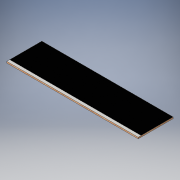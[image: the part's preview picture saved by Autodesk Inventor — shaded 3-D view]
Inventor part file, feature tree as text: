
AUTODESK INVENTOR PART (.ipt)
format: ipt  version: 2016 (Build 200138000, 138)  size: 103,424 bytes
history: native  units: in
note: dims shown in document units (in); Inventor stores cm internally (conversion verified against a paired STEP export)
features: extrude x2, sketch x2
ambient origin geometry x8: Origin, YZ Plane, XZ Plane, XY Plane, X Axis, Y Axis, Z Axis, Center Point
bodies: Solid1 (feature_tree)
feature tree (4):
  extrude  "Extrusion1"  Depth=12.0in
  extrude  "Extrusion2"  Depth=1.0in
  sketch  "Sketch1"  dims[d0=45.0in d1=12.0in]
  sketch  "Sketch2"  dims[d2=0.5in d3=0.0in d4=1.0in d5=0.001in d6=0.0in]
